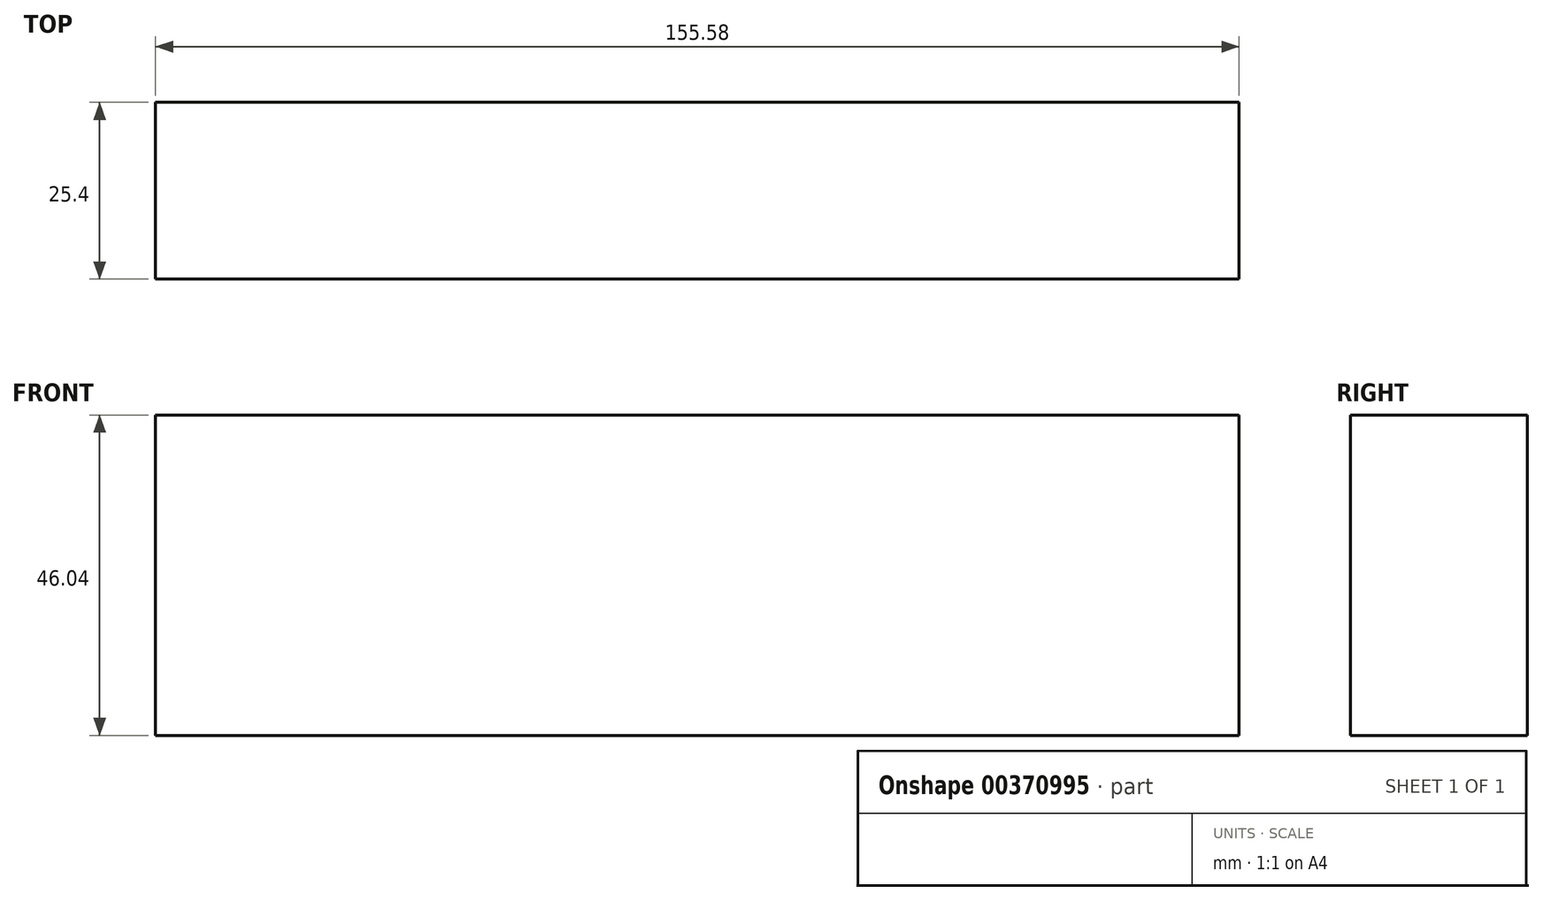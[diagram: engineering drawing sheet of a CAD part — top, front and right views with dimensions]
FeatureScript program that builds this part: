
annotation { "Feature Type Name" : "Feature", "Feature Type Description" : "" }
export const myFeature = defineFeature(function(context is Context, id is Id, definition is map)
    precondition{}
    {
        {
            var Q0;
            Q0=qCreatedBy(makeId("Front.planeOp"),FACE);
            var sketch = newSketch(context, id + "F0", { "sketchPlane" : qUnion([Q0])});
            skLineSegment(sketch, "E0.bottom", {"start": v(77.79, -23.02) * mm, "end": v(-77.79, -23.02) * mm});
            skLineSegment(sketch, "E0.top", {"start": v(77.79, 23.02) * mm, "end": v(-77.79, 23.02) * mm});
            skLineSegment(sketch, "E0.left", {"start": v(77.79, -23.02) * mm, "end": v(77.79, 23.02) * mm});
            skLineSegment(sketch, "E0.right", {"start": v(-77.79, -23.02) * mm, "end": v(-77.79, 23.02) * mm});
            skPoint(sketch, "E0.middle", {"position": v(0, 0) * mm});
            skLineSegment(sketch, "E1.bottom", {"start": v(-77.79, 23.02) * mm, "end": v(-41.27, 23.02) * mm});
            skLineSegment(sketch, "E1.top", {"start": v(-77.79, 53.18) * mm, "end": v(-41.28, 53.18) * mm});
            skLineSegment(sketch, "E1.left", {"start": v(-77.79, 23.02) * mm, "end": v(-77.79, 53.18) * mm});
            skLineSegment(sketch, "E1.right", {"start": v(-41.27, 23.02) * mm, "end": v(-41.28, 53.18) * mm});
            skSolve(sketch);
        }
        {
            var Q0;
            Q0=makeQuery(id+"F0.imprint","IMPRINT",FACE,{"disambiguationData":[TD([[makeQuery(id+"F0.imprint","IMPRINT",EDGE,{"derivedFrom":sQuery(id+"F0.wireOp",EDGE,"E1.bottom")}),1.0]])]});
            var Q1;
            Q1=makeQuery(id+"F0.imprint","IMPRINT",FACE,{"disambiguationData":[TD([[makeQuery(id+"F0.imprint","IMPRINT",EDGE,{"derivedFrom":sQuery(id+"F0.wireOp",EDGE,"E0.bottom")}),-1.0]])]});
            extrude(context, id + "F1", {"entities" : qUnion([Q0, Q1]), "depth" : 25.4 * mm});
        }
    });
